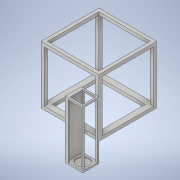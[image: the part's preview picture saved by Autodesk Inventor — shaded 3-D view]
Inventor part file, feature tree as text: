
AUTODESK INVENTOR PART (.ipt)
format: ipt  version: 2021 (Build 250183000, 183)  size: 433,664 bytes
history: native  units: mm
features: sketch x31, extrude x30
ambient origin geometry x8: Origin, YZ Plane, XZ Plane, XY Plane, X Axis, Y Axis, Z Axis, Center Point
bodies: Solid1 (feature_tree)
feature tree (61):
  extrude  "Extrusion1"  Depth=380.0mm
  extrude  "Extrusion2"  Depth=30.0mm
  extrude  "Extrusion3"  Depth=30.0mm
  extrude  "Extrusion4"  Depth=30.0mm TaperAngle=0.0deg
  extrude  "Extrusion5"  Depth=30.0mm
  extrude  "Extrusion6"  Depth=30.0mm
  extrude  "Extrusion7"  Depth=600.0mm TaperAngle=0.0deg
  extrude  "Extrusion8"  Depth=15.0mm TaperAngle=0.0deg
  extrude  "Extrusion9"  Depth=320.0mm
  extrude  "Extrusion10"  Depth=10.0mm
  extrude  "Extrusion11"  Depth=10.0mm TaperAngle=0.0deg
  extrude  "Extrusion13"  Depth=10.0mm
  extrude  "Extrusion14"  Depth=10.0mm
  extrude  "Extrusion15"  Depth=10.0mm TaperAngle=0.0deg
  extrude  "Extrusion16"  Depth=100.0mm
  extrude  "Extrusion17"  Depth=10.0mm
  extrude  "Extrusion19"  Depth=10.0mm
  extrude  "Extrusion20"  Depth=10.0mm TaperAngle=0.0deg
  extrude  "Extrusion21"  Depth=100.0mm TaperAngle=0.0deg
  extrude  "Extrusion22"  Depth=10.0mm
  extrude  "Extrusion23"  Depth=20.0mm
  extrude  "Extrusion26"  Depth=20.0mm TaperAngle=0.0deg
  extrude  "Extrusion30"  Depth=80.0mm TaperAngle=0.0deg
  extrude  "Extrusion31"  Depth=80.0mm TaperAngle=0.0deg
  extrude  "Extrusion32"  Depth=90.0mm TaperAngle=0.0deg
  extrude  "Extrusion33"  Depth=10.0mm TaperAngle=0.0deg
  extrude  "Extrusion34"  Depth=120.0mm TaperAngle=0.0deg
  extrude  "Extrusion35"  Depth=90.0mm TaperAngle=0.0deg
  extrude  "Extrusion36"  Depth=10.0mm TaperAngle=0.0deg
  sketch  "Sketch41"  dims[d102=10.0mm d103=100.0mm d104=0.0mm]
  extrude  "Extrusion37"  Depth=100.0mm TaperAngle=0.0deg
  sketch  "Sketch1"  dims[d0=380.0mm d1=380.0mm]
  sketch  "Sketch2"  dims[d2=380.0mm d3=0.0mm d4=30.0mm]
  sketch  "Sketch3"  dims[d5=30.0mm d6=30.0mm]
  sketch  "Sketch4"  dims[d7=30.0mm d8=600.0mm d9=0.0mm]
  sketch  "Sketch5"  dims[d10=30.0mm d11=30.0mm]
  sketch  "Sketch6"  dims[d12=30.0mm d13=30.0mm]
  sketch  "Sketch7"  dims[d14=600.0mm d15=0.0mm d16=600.0mm d17=0.0mm]
  sketch  "Sketch8"  dims[d18=15.0mm d19=0.0mm d20=15.0mm d21=0.0mm]
  sketch  "Sketch9"  dims[d22=15.0mm d23=0.0mm d24=320.0mm]
  sketch  "Sketch10"  dims[d25=15.0mm d26=0.0mm d27=10.0mm]
  sketch  "Sketch11"  dims[d28=10.0mm d29=900.0mm d30=0.0mm]
  sketch  "Sketch13"  dims[d31=10.0mm d32=10.0mm]
  sketch  "Sketch14"  dims[d33=900.0mm d34=0.0mm d35=10.0mm]
  sketch  "Sketch15"  dims[d36=10.0mm d37=900.0mm d38=0.0mm]
  sketch  "Sketch16"  dims[d41=100.0mm d42=500.0mm]
  sketch  "Sketch17"  dims[d43=100.0mm d44=0.0mm d45=10.0mm]
  sketch  "Sketch19"  dims[d46=10.0mm d47=10.0mm]
  sketch  "Sketch20"  dims[d48=10.0mm d49=900.0mm d50=0.0mm]
  sketch  "Sketch21"  dims[d51=10.0mm d52=100.0mm d53=0.0mm]
  sketch  "Sketch22"  dims[d54=10.0mm d55=10.0mm]
  sketch  "Sketch23"  dims[d56=10.0mm d57=20.0mm]
  sketch  "Sketch26"  dims[d58=100.0mm d59=0.0mm d60=20.0mm d61=0.0mm]
  sketch  "Sketch30"  dims[d65=80.0mm d66=8900.0mm d67=0.0mm]
  sketch  "Sketch31"  dims[d68=8900.0mm d69=0.0mm d70=80.0mm d71=0.0mm]
  sketch  "Sketch32"  dims[d72=20.0mm d73=90.0mm d74=0.0mm]
  sketch  "Sketch33"  dims[d75=20.0mm d76=10.0mm d77=0.0mm]
  sketch  "Sketch34"  dims[d86=100.0mm d87=120.0mm d88=0.0mm]
  sketch  "Sketch35"  dims[d96=120.0mm d97=90.0mm d98=0.0mm]
  sketch  "Sketch36"  dims[d99=10.0mm d100=200.0mm d101=0.0mm]
  sketch  "Sketch42"  dims[d105=10.0mm d106=100.0mm d107=0.0mm d108=10.0mm d109=100.0mm d110=0.0mm d111=100.0mm d112=0.0mm d113=78.0mm d114=5.0mm d115=0.0mm d119=10.0mm d120=10.0mm d121=0.0mm d79=0.5mm d80=0.872665mm d81=0.5mm d82=0.872665mm]
